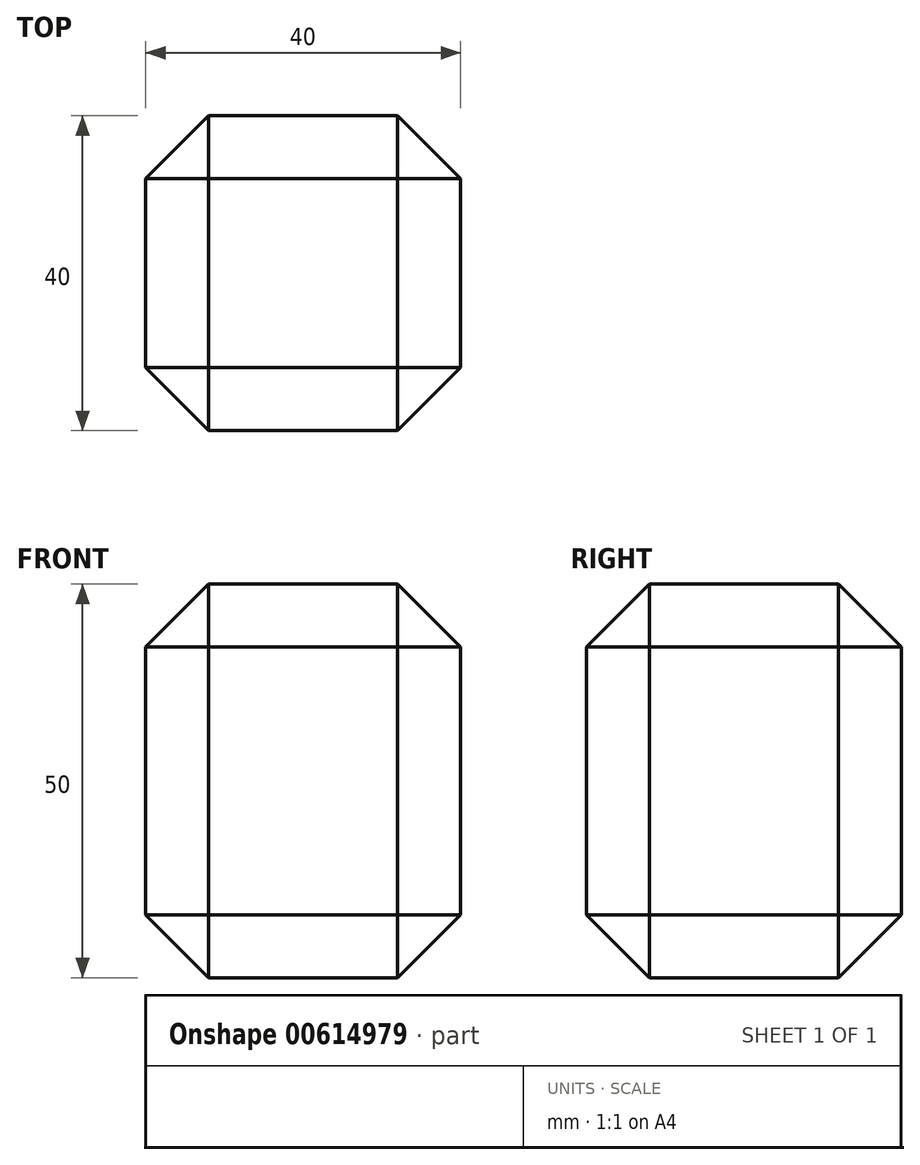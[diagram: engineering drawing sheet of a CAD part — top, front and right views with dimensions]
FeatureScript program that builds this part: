
annotation { "Feature Type Name" : "Feature", "Feature Type Description" : "" }
export const myFeature = defineFeature(function(context is Context, id is Id, definition is map)
    precondition{}
    {
        {
            var Q0;
            Q0=qCreatedBy(makeId("Top.planeOp"),FACE);
            var sketch = newSketch(context, id + "F0", { "sketchPlane" : qUnion([Q0])});
            skLineSegment(sketch, "E0.bottom", {"start": v(-28.15, -19.57) * mm, "end": v(-68.15, -19.57) * mm});
            skLineSegment(sketch, "E0.top", {"start": v(-28.15, 20.43) * mm, "end": v(-68.15, 20.43) * mm});
            skLineSegment(sketch, "E0.left", {"start": v(-28.15, -19.57) * mm, "end": v(-28.15, 20.43) * mm});
            skLineSegment(sketch, "E0.right", {"start": v(-68.15, -19.57) * mm, "end": v(-68.15, 20.43) * mm});
            skPoint(sketch, "E0.middle", {"position": v(-48.15, 0.43) * mm});
            skSolve(sketch);
        }
        {
            var Q0;
            Q0=makeQuery(id+"F0.imprint","IMPRINT",FACE,{"disambiguationData":[TD([[makeQuery(id+"F0.imprint","IMPRINT",EDGE,{"derivedFrom":sQuery(id+"F0.wireOp",EDGE,"E0.bottom")}),-1.0]])]});
            extrude(context, id + "F1", {"entities" : qUnion([Q0]), "depth" : 50 * mm, "offsetDistance" : 25 * mm});
        }
        {
            var Q0;
            Q0=makeQuery(id+"F1.opExtrude","SWEPT_FACE",FACE,{"disambiguationData":[OSD([sQuery(id+"F0.wireOp",EDGE,"E0.left")])]});
            var Q1;
            Q1=makeQuery(id+"F1.opExtrude","SWEPT_FACE",FACE,{"disambiguationData":[OSD([sQuery(id+"F0.wireOp",EDGE,"E0.top")])]});
            var Q2;
            Q2=makeQuery(id+"F1.opExtrude","SWEPT_FACE",FACE,{"disambiguationData":[OSD([sQuery(id+"F0.wireOp",EDGE,"E0.right")])]});
            var Q3;
            Q3=makeQuery(id+"F1.opExtrude","SWEPT_FACE",FACE,{"disambiguationData":[OSD([sQuery(id+"F0.wireOp",EDGE,"E0.bottom")])]});
            chamfer(context, id + "F2", {"entities" : qUnion([Q0, Q1, Q2, Q3]), "width" : 8 * mm, "tangentPropagation" : true});
        }
    });
